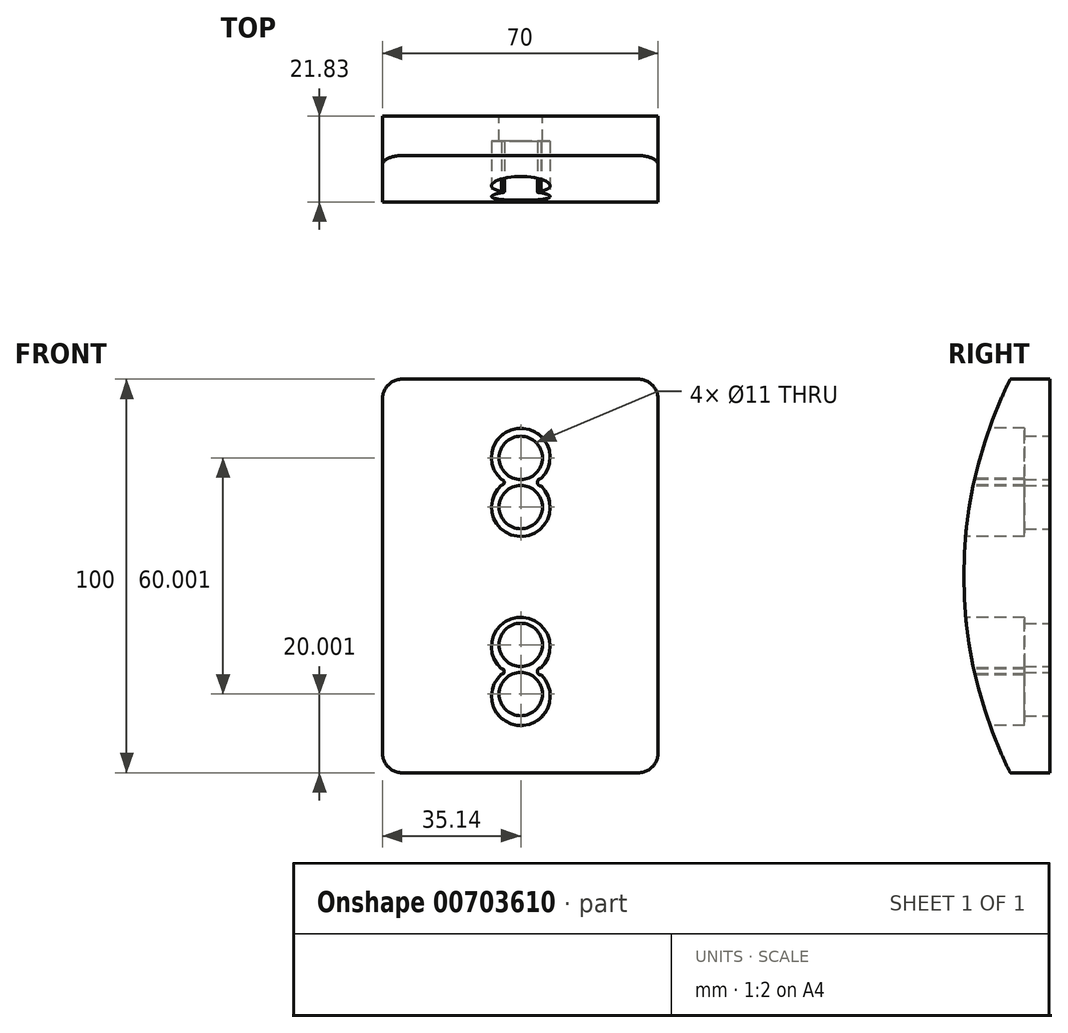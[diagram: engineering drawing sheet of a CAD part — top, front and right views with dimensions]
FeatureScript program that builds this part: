
annotation { "Feature Type Name" : "Feature", "Feature Type Description" : "" }
export const myFeature = defineFeature(function(context is Context, id is Id, definition is map)
    precondition{}
    {
        {
            var Q0;
            Q0=qCreatedBy(makeId("Front.planeOp"),FACE);
            var sketch = newSketch(context, id + "F0", { "sketchPlane" : qUnion([Q0])});
            skLineSegment(sketch, "E0.bottom", {"start": v(-35.14, 53.76) * mm, "end": v(34.86, 53.76) * mm});
            skLineSegment(sketch, "E0.top", {"start": v(-35.14, -46.24) * mm, "end": v(34.86, -46.24) * mm});
            skLineSegment(sketch, "E0.left", {"start": v(-35.14, 53.76) * mm, "end": v(-35.14, -46.24) * mm});
            skLineSegment(sketch, "E0.right", {"start": v(34.86, 53.76) * mm, "end": v(34.86, -46.24) * mm});
            skSolve(sketch);
        }
        {
            var Q0;
            Q0=makeQuery(id+"F0.imprint","IMPRINT",FACE,{"disambiguationData":[TD([[makeQuery(id+"F0.imprint","IMPRINT",EDGE,{"derivedFrom":sQuery(id+"F0.wireOp",EDGE,"E0.bottom")}),-1.0]])]});
            extrude(context, id + "F1", {"entities" : qUnion([Q0]), "depth" : 10 * mm, "offsetDistance" : 25 * mm});
        }
        {
            var Q0;
            Q0=makeQuery(id+"F1.opExtrude","SWEPT_FACE",FACE,{"disambiguationData":[OSD([sQuery(id+"F0.wireOp",EDGE,"E0.right")])]});
            var sketch = newSketch(context, id + "F2", { "sketchPlane" : qUnion([Q0])});
            skArc(sketch, "E1", {"start": v(-10, 53.76) * mm, "mid": v(-21.83, 3.76) * mm, "end": v(-10, -46.24) * mm});
            skSolve(sketch);
        }
        {
            var Q0;
            Q0=makeQuery(id+"F2.imprint","IMPRINT",FACE,{"disambiguationData":[TD([[makeQuery(id+"F2.imprint","IMPRINT",EDGE,{"derivedFrom":sQuery(id+"F2.wireOp",EDGE,"E1")}),1.0]])]});
            extrude(context, id + "F3", {"entities" : qUnion([Q0]), "operationType" : NewBodyOperationType.ADD, "oppositeDirection" : true, "depth" : 70 * mm, "offsetDistance" : 25 * mm});
        }
        {
            var Q0;
            Q0=makeQuery(id+"F1.opExtrude","SWEPT_EDGE",EDGE,{"disambiguationData":[OSD([sQuery(id+"F0.wireOp",EDGE,"E0.bottom"),sQuery(id+"F0.wireOp",EDGE,"E0.right")])]});
            var Q1;
            Q1=makeQuery(id+"F1.opExtrude","SWEPT_EDGE",EDGE,{"disambiguationData":[OSD([sQuery(id+"F0.wireOp",EDGE,"E0.bottom"),sQuery(id+"F0.wireOp",EDGE,"E0.left")])]});
            var Q2;
            Q2=makeQuery(id+"F1.opExtrude","SWEPT_EDGE",EDGE,{"disambiguationData":[OSD([sQuery(id+"F0.wireOp",EDGE,"E0.top"),sQuery(id+"F0.wireOp",EDGE,"E0.right")])]});
            var Q3;
            Q3=makeQuery(id+"F1.opExtrude","SWEPT_EDGE",EDGE,{"disambiguationData":[OSD([sQuery(id+"F0.wireOp",EDGE,"E0.top"),sQuery(id+"F0.wireOp",EDGE,"E0.left")])]});
            fillet(context, id + "F4", {"entities" : qUnion([Q0, Q1, Q2, Q3]), "radius" : 5 * mm, "tangentPropagation" : true, "allowEdgeOverflow" : false});
        }
        {
            var Q0;
            Q0=qCreatedBy(makeId("Front.planeOp"),FACE);
            var sketch = newSketch(context, id + "F5", { "sketchPlane" : qUnion([Q0])});
            skCircle(sketch, "E2", {"center": v(0, 33.76) * mm, "radius": 5 * mm});
            skCircle(sketch, "E3", {"center": v(0, 21.26) * mm, "radius": 5 * mm});
            skCircle(sketch, "E4", {"center": v(0, -13.74) * mm, "radius": 5 * mm});
            skCircle(sketch, "E5", {"center": v(0, -26.24) * mm, "radius": 5 * mm});
            skSolve(sketch);
        }
        {
            var Q0;
            Q0=sQuery(id+"F5.wireOp",VERTEX,"E2.center");
            var Q1;
            Q1=sQuery(id+"F5.wireOp",VERTEX,"E3.center");
            var Q2;
            Q2=sQuery(id+"F5.wireOp",VERTEX,"E4.center");
            var Q3;
            Q3=sQuery(id+"F5.wireOp",VERTEX,"E5.center");
            var Q4;
            Q4=makeQuery(id+"F1.opExtrude","SWEPT_BODY",BODY,{"disambiguationData":[OSD([sQuery(id+"F0.wireOp",EDGE,"E0.bottom"),sQuery(id+"F0.wireOp",EDGE,"E0.top"),sQuery(id+"F0.wireOp",EDGE,"E0.left"),sQuery(id+"F0.wireOp",EDGE,"E0.right")])]});
            hole(context, id + "F6", {"style" : HoleStyle.SIMPLE, "endStyle" : HoleEndStyle.THROUGH, "oppositeDirection" : true, "holeDiameter" : 11 * mm, "majorDiameter" : 5 * mm, "isTappedThrough" : true, "tappedDepth" : 12 * mm, "tapClearance" : 3, "startFromSketch" : true, "locations" : qUnion([Q0, Q1, Q2, Q3]), "scope" : qUnion([Q4])});
        }
        {
            var Q0;
            Q0=qCreatedBy(makeId("Front.planeOp"),FACE);
            cPlane(context, id + "F7", {"entities" : qUnion([Q0]), "cplaneType" : CPlaneType.OFFSET, "offset" : 23.6 * mm, "width" : 150 * mm, "height" : 150 * mm});
        }
        {
            var Q0;
            Q0=qCreatedBy(id+"F7.planeOp",FACE);
            var sketch = newSketch(context, id + "F8", { "sketchPlane" : qUnion([Q0])});
            skArc(sketch, "E6", {"start": v(-4.88, 28.23) * mm, "mid": v(-0.2, 41.3) * mm, "end": v(5.17, 28.5) * mm});
            skArc(sketch, "E7", {"start": v(5.17, 26.63) * mm, "mid": v(-0.15, 13.8) * mm, "end": v(-4.88, 26.86) * mm});
            skArc(sketch, "E8", {"start": v(5.17, 28.5) * mm, "mid": v(4.22, 27.52) * mm, "end": v(5.2, 26.6) * mm});
            skArc(sketch, "E9", {"start": v(-4.88, 28.23) * mm, "mid": v(-4.2, 27.54) * mm, "end": v(-4.88, 26.86) * mm});
            skArc(sketch, "E10", {"start": v(-4.88, -19.8) * mm, "mid": v(-0.2, -6.73) * mm, "end": v(5.17, -19.55) * mm});
            skArc(sketch, "E11", {"start": v(5.17, -21.4) * mm, "mid": v(-0.15, -34.24) * mm, "end": v(-4.88, -21.18) * mm});
            skArc(sketch, "E12", {"start": v(5.17, -19.55) * mm, "mid": v(4.22, -20.51) * mm, "end": v(5.2, -21.44) * mm});
            skArc(sketch, "E13", {"start": v(-4.88, -19.8) * mm, "mid": v(-4.2, -20.5) * mm, "end": v(-4.88, -21.18) * mm});
            skSolve(sketch);
        }
        {
            var Q0;
            Q0 = qSketchRegion(id + "F8", true);
            extrude(context, id + "F9", {"entities" : qUnion([Q0]), "operationType" : NewBodyOperationType.REMOVE, "oppositeDirection" : true, "depth" : 17.2 * mm, "offsetDistance" : 25 * mm});
        }
    });
